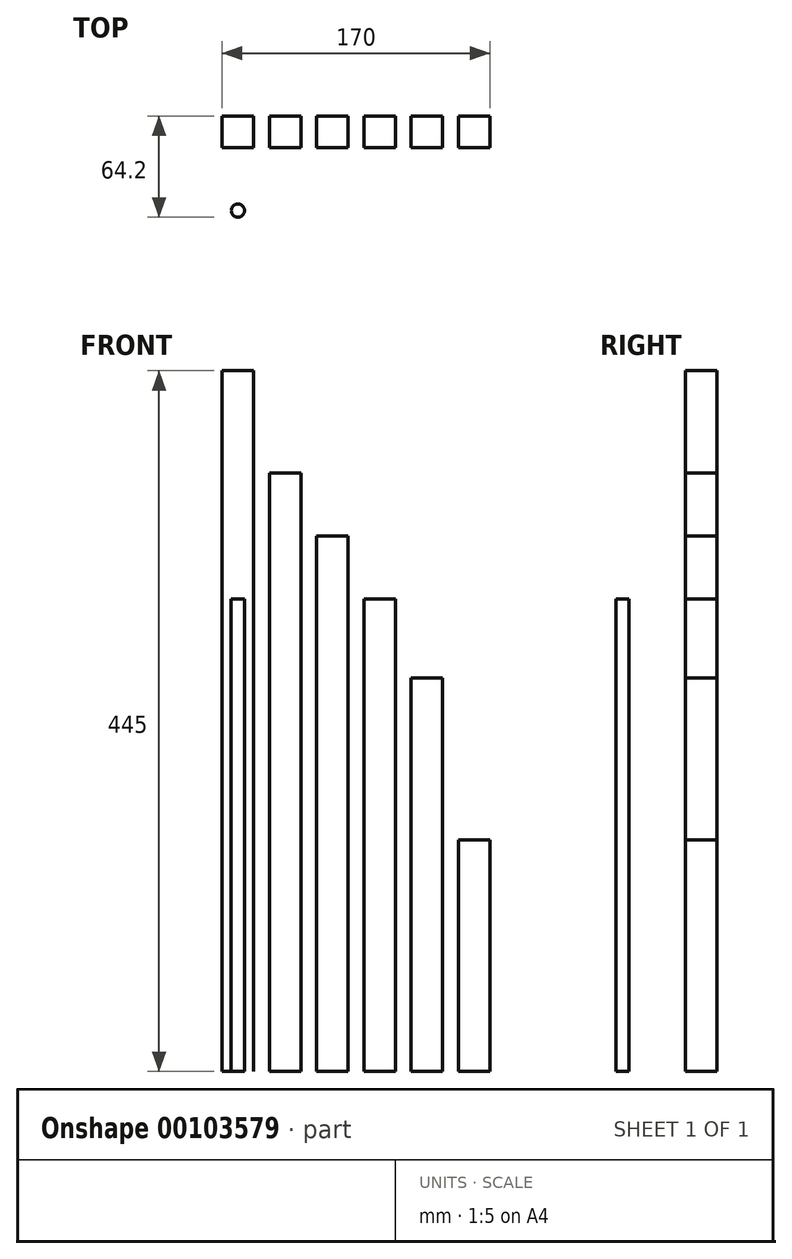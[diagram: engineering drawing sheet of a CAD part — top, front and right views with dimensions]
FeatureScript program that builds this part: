
annotation { "Feature Type Name" : "Feature", "Feature Type Description" : "" }
export const myFeature = defineFeature(function(context is Context, id is Id, definition is map)
    precondition{}
    {
        {
            var Q0;
            Q0=qCreatedBy(makeId("Top.planeOp"),FACE);
            var sketch = newSketch(context, id + "F0", { "sketchPlane" : qUnion([Q0])});
            skLineSegment(sketch, "E0.bottom", {"start": v(10, 10) * mm, "end": v(-10, 10) * mm});
            skLineSegment(sketch, "E0.top", {"start": v(10, -10) * mm, "end": v(-10, -10) * mm});
            skLineSegment(sketch, "E0.left", {"start": v(10, 10) * mm, "end": v(10, -10) * mm});
            skLineSegment(sketch, "E0.right", {"start": v(-10, 10) * mm, "end": v(-10, -10) * mm});
            skPoint(sketch, "E0.middle", {"position": v(0, 0) * mm});
            skLineSegment(sketch, "E1.bottom", {"start": v(20, 10) * mm, "end": v(40, 10) * mm});
            skLineSegment(sketch, "E1.top", {"start": v(20, -10) * mm, "end": v(40, -10) * mm});
            skLineSegment(sketch, "E1.left", {"start": v(20, 10) * mm, "end": v(20, -10) * mm});
            skLineSegment(sketch, "E1.right", {"start": v(40, 10) * mm, "end": v(40, -10) * mm});
            skLineSegment(sketch, "E2.bottom", {"start": v(50, 10) * mm, "end": v(70, 10) * mm});
            skLineSegment(sketch, "E2.top", {"start": v(50, -10) * mm, "end": v(70, -10) * mm});
            skLineSegment(sketch, "E2.left", {"start": v(50, 10) * mm, "end": v(50, -10) * mm});
            skLineSegment(sketch, "E2.right", {"start": v(70, 10) * mm, "end": v(70, -10) * mm});
            skLineSegment(sketch, "E3.bottom", {"start": v(80, 10) * mm, "end": v(100, 10) * mm});
            skLineSegment(sketch, "E3.top", {"start": v(80, -10) * mm, "end": v(100, -10) * mm});
            skLineSegment(sketch, "E3.left", {"start": v(80, 10) * mm, "end": v(80, -10) * mm});
            skLineSegment(sketch, "E3.right", {"start": v(100, 10) * mm, "end": v(100, -10) * mm});
            skCircle(sketch, "E4", {"center": v(0, -50) * mm, "radius": 4.2 * mm});
            skLineSegment(sketch, "E5.bottom", {"start": v(110, 10) * mm, "end": v(130, 10) * mm});
            skLineSegment(sketch, "E5.top", {"start": v(110, -10) * mm, "end": v(130, -10) * mm});
            skLineSegment(sketch, "E5.left", {"start": v(110, 10) * mm, "end": v(110, -10) * mm});
            skLineSegment(sketch, "E5.right", {"start": v(130, 10) * mm, "end": v(130, -10) * mm});
            skLineSegment(sketch, "E6.bottom", {"start": v(140, 10) * mm, "end": v(160, 10) * mm});
            skLineSegment(sketch, "E6.top", {"start": v(140, -10) * mm, "end": v(160, -10) * mm});
            skLineSegment(sketch, "E6.left", {"start": v(140, 10) * mm, "end": v(140, -10) * mm});
            skLineSegment(sketch, "E6.right", {"start": v(160, 10) * mm, "end": v(160, -10) * mm});
            skSolve(sketch);
        }
        {
            var Q0;
            Q0=makeQuery(id+"F0.imprint","IMPRINT",FACE,{"disambiguationData":[TD([[makeQuery(id+"F0.imprint","IMPRINT",EDGE,{"derivedFrom":sQuery(id+"F0.wireOp",EDGE,"E0.bottom")}),1.0]])]});
            extrude(context, id + "F1", {"entities" : qUnion([Q0]), "depth" : (345 + 100) * mm});
        }
        {
            var Q0;
            Q0=makeQuery(id+"F0.imprint","IMPRINT",FACE,{"disambiguationData":[TD([[makeQuery(id+"F0.imprint","IMPRINT",EDGE,{"derivedFrom":sQuery(id+"F0.wireOp",EDGE,"E1.bottom")}),-1.0]])]});
            extrude(context, id + "F2", {"entities" : qUnion([Q0]), "depth" : 380 * mm});
        }
        {
            var Q0;
            Q0=makeQuery(id+"F0.imprint","IMPRINT",FACE,{"disambiguationData":[TD([[makeQuery(id+"F0.imprint","IMPRINT",EDGE,{"derivedFrom":sQuery(id+"F0.wireOp",EDGE,"E2.bottom")}),-1.0]])]});
            extrude(context, id + "F3", {"entities" : qUnion([Q0]), "depth" : 340 * mm});
        }
        {
            var Q0;
            Q0=makeQuery(id+"F0.imprint","IMPRINT",FACE,{"disambiguationData":[TD([[makeQuery(id+"F0.imprint","IMPRINT",EDGE,{"derivedFrom":sQuery(id+"F0.wireOp",EDGE,"E3.bottom")}),-1.0]])]});
            extrude(context, id + "F4", {"entities" : qUnion([Q0]), "depth" : 300 * mm});
        }
        {
            var Q0;
            Q0=makeQuery(id+"F0.imprint","IMPRINT",FACE,{"disambiguationData":[TD([[makeQuery(id+"F0.imprint","IMPRINT",EDGE,{"derivedFrom":sQuery(id+"F0.wireOp",EDGE,"E4")}),1.0]])]});
            extrude(context, id + "F5", {"entities" : qUnion([Q0]), "depth" : 300 * mm});
        }
        {
            var Q0;
            Q0=makeQuery(id+"F0.imprint","IMPRINT",FACE,{"disambiguationData":[TD([[makeQuery(id+"F0.imprint","IMPRINT",EDGE,{"derivedFrom":sQuery(id+"F0.wireOp",EDGE,"E5.bottom")}),-1.0]])]});
            extrude(context, id + "F6", {"entities" : qUnion([Q0]), "depth" : 250 * mm});
        }
        {
            var Q0;
            Q0=makeQuery(id+"F0.imprint","IMPRINT",FACE,{"disambiguationData":[TD([[makeQuery(id+"F0.imprint","IMPRINT",EDGE,{"derivedFrom":sQuery(id+"F0.wireOp",EDGE,"E6.bottom")}),-1.0]])]});
            extrude(context, id + "F7", {"entities" : qUnion([Q0]), "depth" : 147 * mm});
        }
    });
